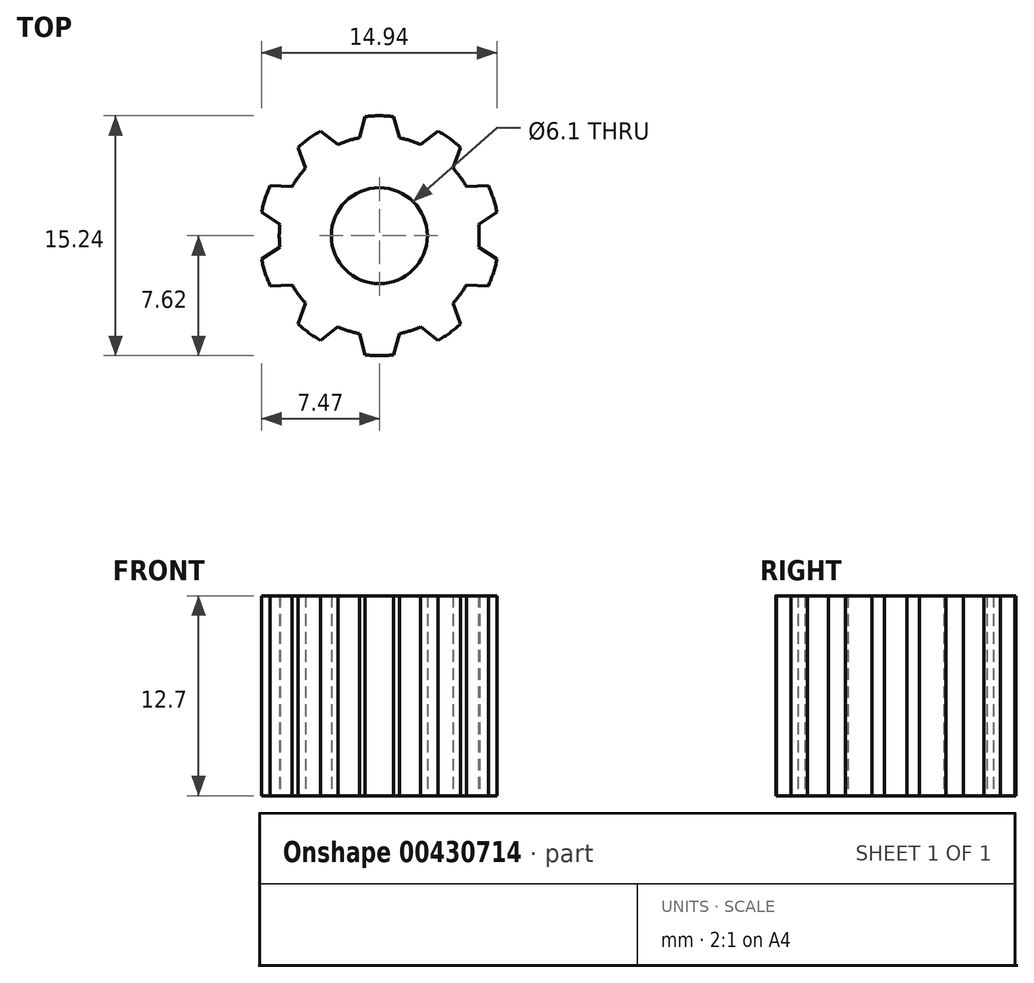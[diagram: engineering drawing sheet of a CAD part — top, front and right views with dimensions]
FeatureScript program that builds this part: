
annotation { "Feature Type Name" : "Feature", "Feature Type Description" : "" }
export const myFeature = defineFeature(function(context is Context, id is Id, definition is map)
    precondition{}
    {
        {
            var Q0;
            Q0=qCreatedBy(makeId("Top.planeOp"),FACE);
            var sketch = newSketch(context, id + "F0", { "sketchPlane" : qUnion([Q0])});
            skCircle(sketch, "E0", {"center": v(0, 0) * mm, "radius": 7.62 * mm});
            skCircle(sketch, "E1", {"center": v(0, 0) * mm, "radius": 3.05 * mm});
            skCircle(sketch, "E2", {"center": v(0, 0) * mm, "radius": 6.35 * mm});
            skLineSegment(sketch, "E3", {"start": v(-1.27, 6.22) * mm, "end": v(-0.89, 7.57) * mm});
            skLineSegment(sketch, "E4", {"start": v(1.27, 6.22) * mm, "end": v(0.89, 7.57) * mm});
            skLineSegment(sketch, "E5.1.0", {"start": v(-4.68, 4.29) * mm, "end": v(-5.17, 5.6) * mm});
            skLineSegment(sketch, "E5.1.1", {"start": v(-2.63, 5.78) * mm, "end": v(-3.73, 6.65) * mm});
            skLineSegment(sketch, "E5.2.0", {"start": v(-6.3, 0.71) * mm, "end": v(-7.47, 1.5) * mm});
            skLineSegment(sketch, "E5.2.1", {"start": v(-5.52, 3.13) * mm, "end": v(-6.92, 3.18) * mm});
            skLineSegment(sketch, "E5.3.0", {"start": v(-5.52, -3.13) * mm, "end": v(-6.92, -3.18) * mm});
            skLineSegment(sketch, "E5.3.1", {"start": v(-6.3, -0.71) * mm, "end": v(-7.47, -1.5) * mm});
            skLineSegment(sketch, "E5.4.0", {"start": v(-2.63, -5.78) * mm, "end": v(-3.73, -6.65) * mm});
            skLineSegment(sketch, "E5.4.1", {"start": v(-4.68, -4.29) * mm, "end": v(-5.17, -5.6) * mm});
            skLineSegment(sketch, "E5.5.0", {"start": v(1.27, -6.22) * mm, "end": v(0.89, -7.57) * mm});
            skLineSegment(sketch, "E5.5.1", {"start": v(-1.27, -6.22) * mm, "end": v(-0.89, -7.57) * mm});
            skLineSegment(sketch, "E5.6.0", {"start": v(4.68, -4.29) * mm, "end": v(5.17, -5.6) * mm});
            skLineSegment(sketch, "E5.6.1", {"start": v(2.63, -5.78) * mm, "end": v(3.73, -6.65) * mm});
            skLineSegment(sketch, "E5.7.0", {"start": v(6.3, -0.71) * mm, "end": v(7.47, -1.5) * mm});
            skLineSegment(sketch, "E5.7.1", {"start": v(5.52, -3.13) * mm, "end": v(6.92, -3.18) * mm});
            skLineSegment(sketch, "E5.8.0", {"start": v(5.52, 3.13) * mm, "end": v(6.92, 3.18) * mm});
            skLineSegment(sketch, "E5.8.1", {"start": v(6.3, 0.71) * mm, "end": v(7.47, 1.5) * mm});
            skLineSegment(sketch, "E5.9.0", {"start": v(2.63, 5.78) * mm, "end": v(3.73, 6.65) * mm});
            skLineSegment(sketch, "E5.9.1", {"start": v(4.68, 4.29) * mm, "end": v(5.17, 5.6) * mm});
            skSolve(sketch);
        }
        {
            var Q0;
            {var subQ0=sQuery(id+"F0.wireOp",EDGE,"E5.8.0");Q0=makeQuery(id+"F0.imprint","IMPRINT",FACE,{"disambiguationData":[TD([[makeQuery(id+"F0.imprint","IMPRINT",EDGE,{"derivedFrom":subQ0}),-1.0]])]});}
            var Q1;
            {var subQ0=sQuery(id+"F0.wireOp",EDGE,"E5.9.0");Q1=makeQuery(id+"F0.imprint","IMPRINT",FACE,{"disambiguationData":[TD([[makeQuery(id+"F0.imprint","IMPRINT",EDGE,{"derivedFrom":subQ0}),-1.0]])]});}
            var Q2;
            {var subQ0=sQuery(id+"F0.wireOp",EDGE,"E3");Q2=makeQuery(id+"F0.imprint","IMPRINT",FACE,{"disambiguationData":[TD([[makeQuery(id+"F0.imprint","IMPRINT",EDGE,{"derivedFrom":subQ0}),-1.0]])]});}
            var Q3;
            {var subQ0=sQuery(id+"F0.wireOp",EDGE,"E5.1.0");Q3=makeQuery(id+"F0.imprint","IMPRINT",FACE,{"disambiguationData":[TD([[makeQuery(id+"F0.imprint","IMPRINT",EDGE,{"derivedFrom":subQ0}),-1.0]])]});}
            var Q4;
            {var subQ0=sQuery(id+"F0.wireOp",EDGE,"E5.2.0");Q4=makeQuery(id+"F0.imprint","IMPRINT",FACE,{"disambiguationData":[TD([[makeQuery(id+"F0.imprint","IMPRINT",EDGE,{"derivedFrom":subQ0}),-1.0]])]});}
            var Q5;
            {var subQ0=sQuery(id+"F0.wireOp",EDGE,"E5.3.0");Q5=makeQuery(id+"F0.imprint","IMPRINT",FACE,{"disambiguationData":[TD([[makeQuery(id+"F0.imprint","IMPRINT",EDGE,{"derivedFrom":subQ0}),-1.0]])]});}
            var Q6;
            {var subQ0=sQuery(id+"F0.wireOp",EDGE,"E5.4.0");Q6=makeQuery(id+"F0.imprint","IMPRINT",FACE,{"disambiguationData":[TD([[makeQuery(id+"F0.imprint","IMPRINT",EDGE,{"derivedFrom":subQ0}),-1.0]])]});}
            var Q7;
            {var subQ0=sQuery(id+"F0.wireOp",EDGE,"E5.5.0");Q7=makeQuery(id+"F0.imprint","IMPRINT",FACE,{"disambiguationData":[TD([[makeQuery(id+"F0.imprint","IMPRINT",EDGE,{"derivedFrom":subQ0}),-1.0]])]});}
            var Q8;
            {var subQ0=sQuery(id+"F0.wireOp",EDGE,"E5.6.0");Q8=makeQuery(id+"F0.imprint","IMPRINT",FACE,{"disambiguationData":[TD([[makeQuery(id+"F0.imprint","IMPRINT",EDGE,{"derivedFrom":subQ0}),-1.0]])]});}
            var Q9;
            {var subQ0=sQuery(id+"F0.wireOp",EDGE,"E5.7.0");Q9=makeQuery(id+"F0.imprint","IMPRINT",FACE,{"disambiguationData":[TD([[makeQuery(id+"F0.imprint","IMPRINT",EDGE,{"derivedFrom":subQ0}),-1.0]])]});}
            var Q10;
            Q10=makeQuery(id+"F0.imprint","IMPRINT",FACE,{"disambiguationData":[TD([[makeQuery(id+"F0.imprint","IMPRINT",EDGE,{"derivedFrom":sQuery(id+"F0.wireOp",EDGE,"E1")}),-1.0]])]});
            extrude(context, id + "F1", {"entities" : qUnion([Q0, Q1, Q2, Q3, Q4, Q5, Q6, Q7, Q8, Q9, Q10]), "depth" : 12.7 * mm, "offsetDistance" : 25.4 * mm});
        }
    });
